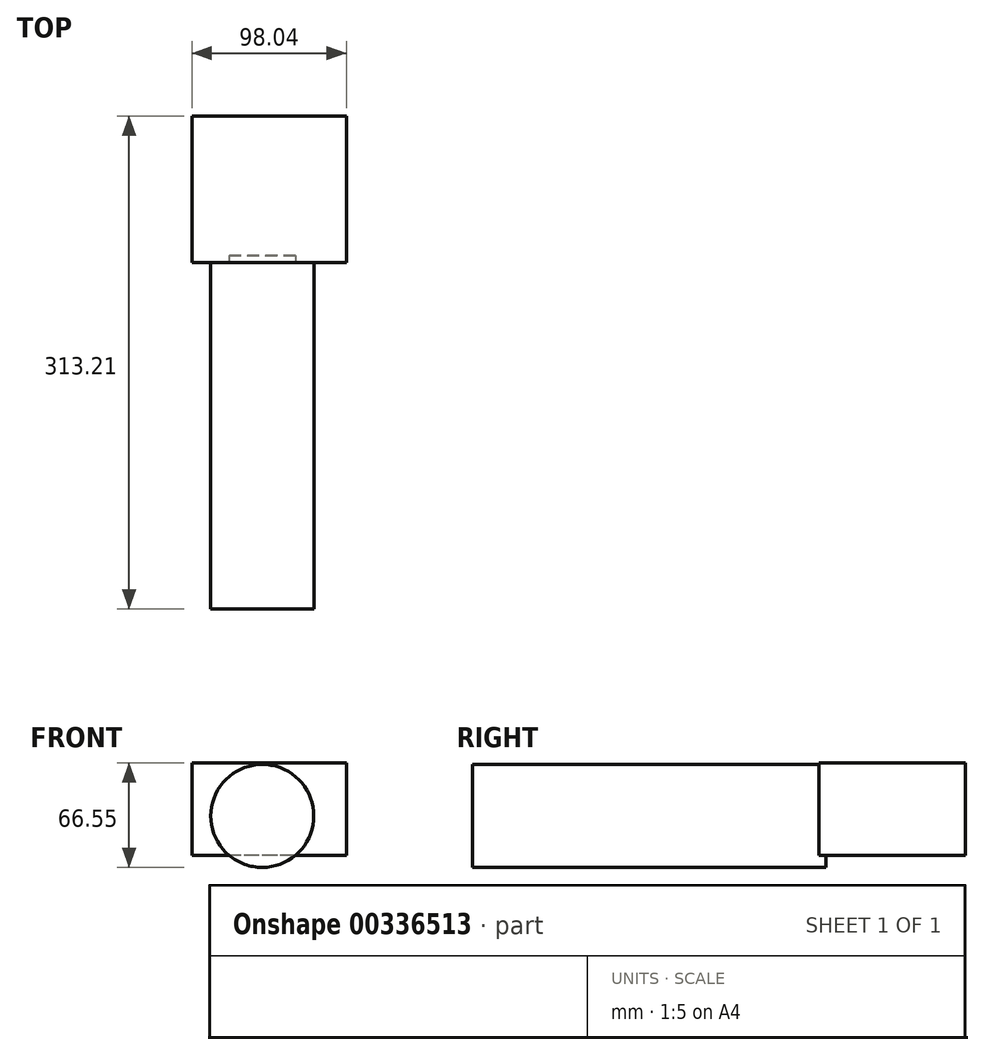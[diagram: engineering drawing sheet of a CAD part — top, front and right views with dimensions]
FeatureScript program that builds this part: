
annotation { "Feature Type Name" : "Feature", "Feature Type Description" : "" }
export const myFeature = defineFeature(function(context is Context, id is Id, definition is map)
    precondition{}
    {
        {
            var Q0;
            Q0=qCreatedBy(makeId("Front.planeOp"),FACE);
            var sketch = newSketch(context, id + "F0", { "sketchPlane" : qUnion([Q0])});
            skLineSegment(sketch, "E0.bottom", {"start": v(53.39, 58.84) * mm, "end": v(-44.65, 58.84) * mm});
            skLineSegment(sketch, "E0.top", {"start": v(53.39, 0) * mm, "end": v(-44.65, 0) * mm});
            skLineSegment(sketch, "E0.left", {"start": v(53.39, 58.84) * mm, "end": v(53.39, 0) * mm});
            skLineSegment(sketch, "E0.right", {"start": v(-44.65, 58.84) * mm, "end": v(-44.65, 0) * mm});
            skSolve(sketch);
        }
        {
            var Q0;
            Q0=makeQuery(id+"F0.imprint","IMPRINT",FACE,{"disambiguationData":[TD([[makeQuery(id+"F0.imprint","IMPRINT",EDGE,{"derivedFrom":sQuery(id+"F0.wireOp",EDGE,"E0.bottom")}),1.0]])]});
            extrude(context, id + "F1", {"entities" : qUnion([Q0]), "depth" : 25.4 * mm});
        }
        {
            var Q0;
            Q0=makeQuery(id+"F1.opExtrude","CAP_FACE",FACE,{"disambiguationData":[OSD([sQuery(id+"F0.wireOp",EDGE,"E0.bottom"),sQuery(id+"F0.wireOp",EDGE,"E0.top"),sQuery(id+"F0.wireOp",EDGE,"E0.left"),sQuery(id+"F0.wireOp",EDGE,"E0.right")])],"isStart":false});
            extrude(context, id + "F2", {"entities" : qUnion([Q0]), "operationType" : NewBodyOperationType.ADD, "depth" : 67.72 * mm});
        }
        {
            var Q0;
            Q0=makeQuery(id+"F2.opExtrude","CAP_FACE",FACE,{"disambiguationData":[OSD([sQuery(id+"F0.wireOp",EDGE,"E0.bottom"),sQuery(id+"F0.wireOp",EDGE,"E0.top"),sQuery(id+"F0.wireOp",EDGE,"E0.left"),sQuery(id+"F0.wireOp",EDGE,"E0.right")])],"isStart":false});
            var sketch = newSketch(context, id + "F3", { "sketchPlane" : qUnion([Q0])});
            skCircle(sketch, "E1", {"center": v(0, 25) * mm, "radius": 32.71 * mm});
            skSolve(sketch);
        }
        {
            var Q0;
            {var subQ0=sQuery(id+"F3.wireOp",EDGE,"E1");var subQ1=makeQuery(id+"F2.opExtrude","CAP_EDGE",EDGE,{"disambiguationData":[OSD([sQuery(id+"F0.wireOp",EDGE,"E0.top")])],"isStart":false});var subQ2=makeQuery(id+"F3.imprint","INTERSECT",VERTEX,{"disambiguationData":[OD(0.0)],"derivedFrom":[subQ1,subQ0]});Q0=makeQuery(id+"F3.imprint","IMPRINT",FACE,{"disambiguationData":[TD([[makeQuery(id+"F3.imprint","IMPRINT",EDGE,{"disambiguationData":[TD([[subQ2,1.0]])],"derivedFrom":subQ0}),1.0]])]});}
            var Q1;
            {var subQ0=sQuery(id+"F3.wireOp",EDGE,"E1");var subQ1=makeQuery(id+"F2.opExtrude","CAP_EDGE",EDGE,{"disambiguationData":[OSD([sQuery(id+"F0.wireOp",EDGE,"E0.top")])],"isStart":false});var subQ2=makeQuery(id+"F3.imprint","INTERSECT",VERTEX,{"disambiguationData":[OD(0.0)],"derivedFrom":[subQ1,subQ0]});Q1=makeQuery(id+"F3.imprint","IMPRINT",FACE,{"disambiguationData":[TD([[makeQuery(id+"F3.imprint","IMPRINT",EDGE,{"disambiguationData":[TD([[subQ2,-1.0]])],"derivedFrom":subQ0}),1.0]])]});}
            extrude(context, id + "F4", {"entities" : qUnion([Q0, Q1]), "operationType" : NewBodyOperationType.ADD, "depth" : 220.1 * mm});
        }
        {
            var Q0;
            Q0=makeQuery(id+"F4.opExtrude","CAP_FACE",FACE,{"disambiguationData":[OSD([sQuery(id+"F3.wireOp",EDGE,"E1")])],"isStart":false});
            var sketch = newSketch(context, id + "F5", { "sketchPlane" : qUnion([Q0])});
            skCircle(sketch, "E2", {"center": v(0, 25) * mm, "radius": 19.17 * mm});
            skSolve(sketch);
        }
        {
            var Q0;
            Q0=makeQuery(id+"F5.imprint","IMPRINT",FACE,{"disambiguationData":[TD([[makeQuery(id+"F5.imprint","IMPRINT",EDGE,{"derivedFrom":sQuery(id+"F5.wireOp",EDGE,"E2")}),1.0]])]});
            extrude(context, id + "F6", {"entities" : qUnion([Q0]), "operationType" : NewBodyOperationType.ADD, "oppositeDirection" : true, "depth" : 130.06 * mm});
        }
        {
            var Q0;
            Q0=makeQuery(id+"F4.opExtrude","CAP_FACE",FACE,{"disambiguationData":[OSD([sQuery(id+"F3.wireOp",EDGE,"E1")])],"isStart":false});
            extrude(context, id + "F7", {"entities" : qUnion([Q0]), "operationType" : NewBodyOperationType.ADD, "oppositeDirection" : true, "depth" : 224.5 * mm});
        }
    });
